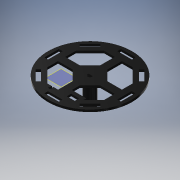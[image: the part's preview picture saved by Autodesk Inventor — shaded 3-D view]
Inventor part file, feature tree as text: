
AUTODESK INVENTOR PART (.ipt)
format: ipt  version: 2018 (Build 220112000, 112)  size: 307,712 bytes
history: native  units: mm
features: extrude x9, sketch x8, other x4, plane x1, fillet x1
ambient origin geometry x8: Origin, YZ Plane, XZ Plane, XY Plane, X Axis, Y Axis, Z Axis, Center Point
bodies: Body1 (feature_tree)
feature tree (23):
  plane  "Work Plane2"
  extrude  "Extrusion9"  Depth=14.75mm
  extrude  "Extrusion10"  Depth=6.25mm
  extrude  "Extrusion12"  Depth=15.0mm TaperAngle=0.0deg
  extrude  "Extrusion13"  Depth=10.0mm TaperAngle=0.0deg
  fillet  "Fillet2"  Radius=10.0mm
  extrude  "Extrusion18"  Depth=10.0mm
  extrude  "Extrusion19"  Depth=20.0mm
  extrude  "Extrusión20"  Depth=10.0mm
  extrude  "Extrusión21"  Depth=0.5mm
  other  "Edición directa1"
  extrude  "Extrusión22"  Depth=0.5mm
  other  "Edición directa2"
  sketch  "Sketch9"  dims[d39=20.0mm d40=14.75mm]
  sketch  "Sketch10"  dims[d41=6.0mm d42=0.0mm d43=6.25mm]
  sketch  "Sketch11"  dims[d44=1.0mm d45=15.0mm d46=0.0mm]
  sketch  "Sketch16"  dims[d48=116.0mm d51=3.0mm d52=0.0mm d55=10.0mm]
  sketch  "Sketch17"  dims[d56=10.0mm d58=10.0mm]
  sketch  "Boceto18"  dims[d59=5.0mm d60=20.0mm]
  sketch  "Boceto19"  dims[d62=10.0mm d63=5.0mm]
  sketch  "Boceto20"  dims[d64=20.0mm d67=5.0mm d68=5.0mm d69=5.0mm d70=20.0mm d71=10.0mm d72=10.0mm d73=20.0mm d74=10.0mm d75=20.0mm d76=15.0mm d77=15.0mm d78=3.0mm d79=0.0mm d80=0.5mm d104=1.0mm d105=1.0mm d106=1.0mm d107=2.0mm d109=3.0mm d110=0.0mm d111=15.0mm d112=6.0mm d113=0.0mm d115=5.0mm d116=3.0mm d117=0.0mm d118=11.0mm d119=6.0mm d120=3.0mm d121=0.0mm d122=0.0mm d123=0.0mm d124=-1.0mm d125=3.0mm d126=0.0mm d127=0.0mm d128=0.0mm d129=27.0mm]
  other  "Desplazar1"
  other  "Desplazar2"
